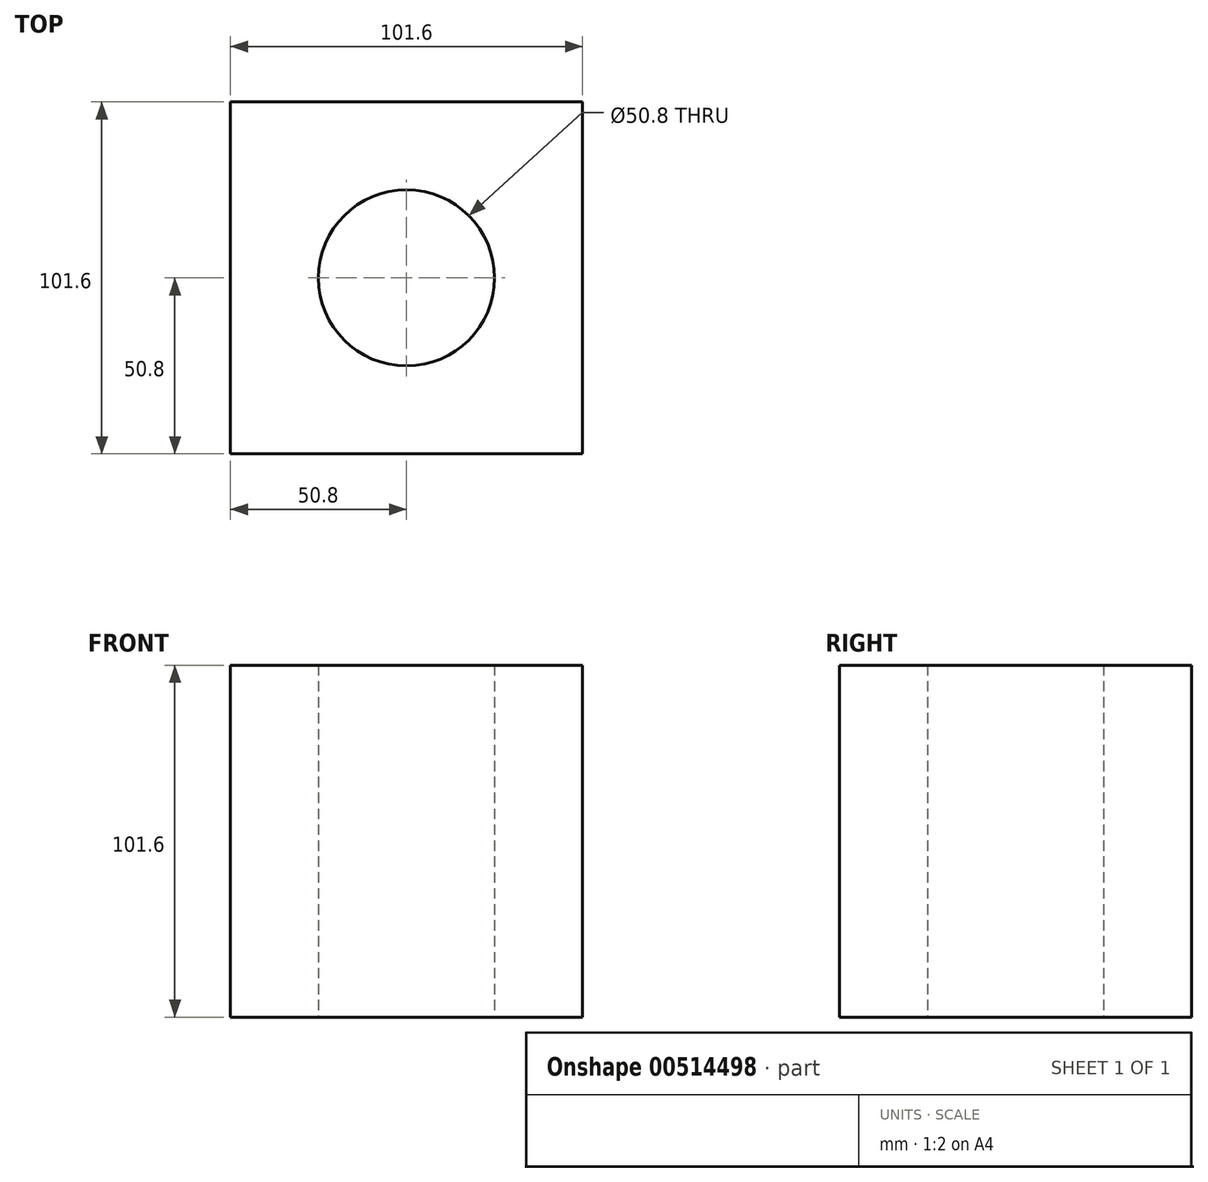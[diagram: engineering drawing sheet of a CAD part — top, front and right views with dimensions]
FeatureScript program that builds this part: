
annotation { "Feature Type Name" : "Feature", "Feature Type Description" : "" }
export const myFeature = defineFeature(function(context is Context, id is Id, definition is map)
    precondition{}
    {
        {
            var Q0;
            Q0=qCreatedBy(makeId("Top.planeOp"),FACE);
            var sketch = newSketch(context, id + "F0", { "sketchPlane" : qUnion([Q0])});
            skLineSegment(sketch, "E0.bottom", {"start": v(50.8, 50.8) * mm, "end": v(-50.8, 50.8) * mm});
            skLineSegment(sketch, "E0.top", {"start": v(50.8, -50.8) * mm, "end": v(-50.8, -50.8) * mm});
            skLineSegment(sketch, "E0.left", {"start": v(50.8, 50.8) * mm, "end": v(50.8, -50.8) * mm});
            skLineSegment(sketch, "E0.right", {"start": v(-50.8, 50.8) * mm, "end": v(-50.8, -50.8) * mm});
            skPoint(sketch, "E0.middle", {"position": v(0, 0) * mm});
            skPoint(sketch, "E1.17.internal.orphan", {"position": v(19.38, 0) * mm});
            skPoint(sketch, "E1.25.internal.orphan", {"position": v(0, -17.21) * mm});
            skPoint(sketch, "E1.36.internal.orphan", {"position": v(-26.07, 0) * mm});
            skPoint(sketch, "E1.39.internal.orphan", {"position": v(-42.78, 0) * mm});
            skPoint(sketch, "E1.6.internal.orphan", {"position": v(0, 10.2) * mm});
            skCircle(sketch, "E2", {"center": v(0, 0) * mm, "radius": 25.4 * mm});
            skSolve(sketch);
        }
        {
            var Q0;
            Q0=makeQuery(id+"F0.imprint","IMPRINT",FACE,{"disambiguationData":[TD([[makeQuery(id+"F0.imprint","IMPRINT",EDGE,{"derivedFrom":sQuery(id+"F0.wireOp",EDGE,"E0.bottom")}),1.0]])]});
            extrude(context, id + "F1", {"entities" : qUnion([Q0]), "depth" : 101.6 * mm});
        }
    });
